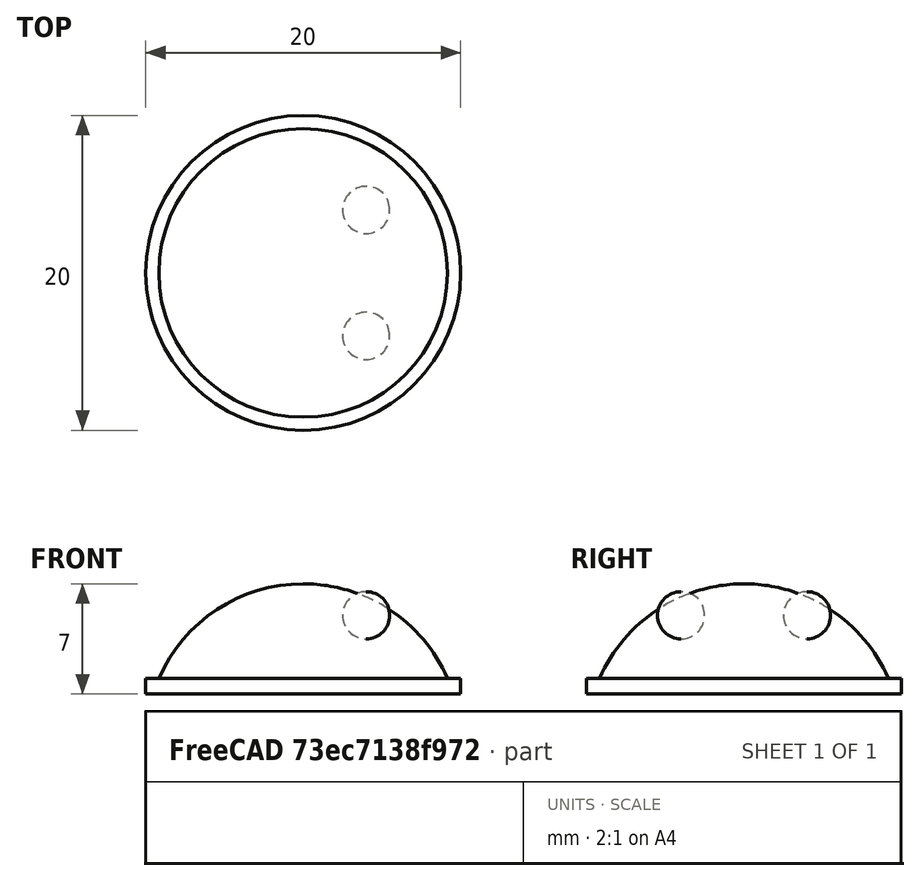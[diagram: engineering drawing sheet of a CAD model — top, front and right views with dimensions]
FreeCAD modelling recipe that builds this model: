
FCSTD DOCUMENT  (FreeCAD 0.21R33694 (Git))
Label: OJT1_T13P02.barret
License: All rights reserved
LicenseURL: http://en.wikipedia.org/wiki/All_rights_reserved
objects: Part::Sphere×3, Part::Cylinder×1, Part::Fuse×1
note: 5 computed .brp shape members not serialized (recipe doc carries the construction recipe); baked Part::Feature solids carry a one-line shape summary decoded from their .brp

FEATURE [Part::Sphere] Sphere  label="Esfera"
  Angle1 = 20
  Angle2 = 90
  Angle3 = 360
  AttacherType = Attacher::AttachEngine3D
  Radius = 10
FEATURE [Part::Cylinder] Cylinder  label="Cilindre"
  Angle = 360
  AttacherType = Attacher::AttachEngine3D
  FirstAngle = 0
  Height = 1
  Placement = pos=(0,0,3) rot=(0,0,1;0rad)
  Radius = 10
  SecondAngle = 0
FEATURE [Part::Sphere] Sphere001  label="Esfera001"
  Angle1 = -90
  Angle2 = 90
  Angle3 = 360
  AttacherType = Attacher::AttachEngine3D
  Placement = pos=(4,-4,8) rot=(0,0,1;0rad)
  Radius = 1.5
FEATURE [Part::Sphere] Sphere002  label="Esfera002"
  Angle1 = -90
  Angle2 = 90
  Angle3 = 360
  AttacherType = Attacher::AttachEngine3D
  Placement = pos=(4,4,8) rot=(0,0,1;0rad)
  Radius = 1.5
FEATURE [Part::Fuse] Fusion
  Base = -> Sphere
  Refine = true
  Tool = -> Cylinder
